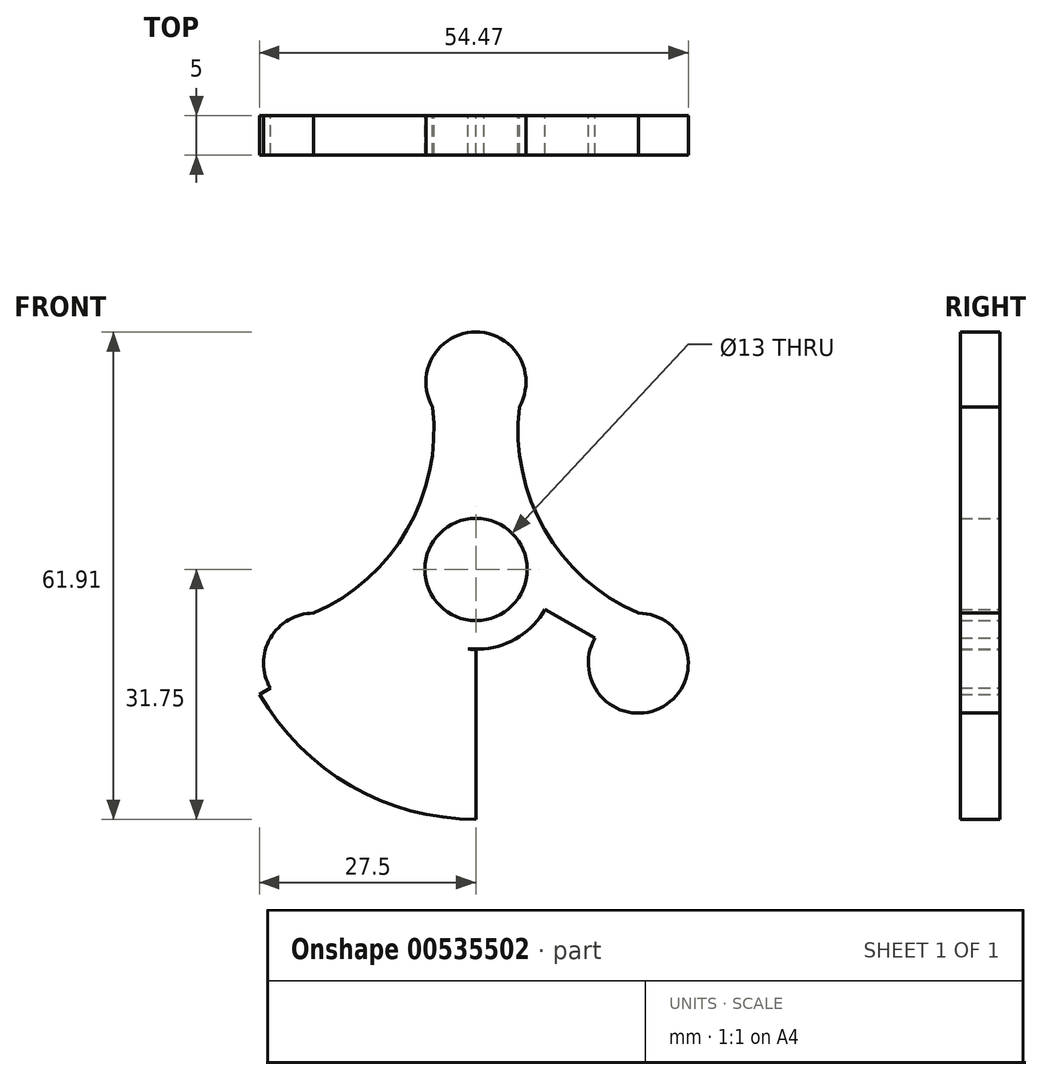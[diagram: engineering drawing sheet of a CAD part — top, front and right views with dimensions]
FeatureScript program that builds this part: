
annotation { "Feature Type Name" : "Feature", "Feature Type Description" : "" }
export const myFeature = defineFeature(function(context is Context, id is Id, definition is map)
    precondition{}
    {
        {
            var Q0;
            Q0=qCreatedBy(makeId("Front.planeOp"),FACE);
            var sketch = newSketch(context, id + "F0", { "sketchPlane" : qUnion([Q0])});
            skCircle(sketch, "E0", {"center": v(0, 0) * mm, "radius": 10.16 * mm});
            skCircle(sketch, "E1", {"center": v(0, 0) * mm, "radius": 31.75 * mm});
            skLineSegment(sketch, "E2", {"start": v(0, 0) * mm, "end": v(0, 31.75) * mm});
            skLineSegment(sketch, "E3", {"start": v(0, 0) * mm, "end": v(0, -31.75) * mm});
            skLineSegment(sketch, "E4", {"start": v(0, 0) * mm, "end": v(-31.75, 0) * mm});
            skLineSegment(sketch, "E5", {"start": v(0, 0) * mm, "end": v(31.75, 0) * mm});
            skLineSegment(sketch, "E6", {"start": v(0, -15.88) * mm, "end": v(0, -31.75) * mm});
            skLineSegment(sketch, "E7", {"start": v(15.88, 0) * mm, "end": v(31.75, 0) * mm});
            skLineSegment(sketch, "E8", {"start": v(0, 31.75) * mm, "end": v(0, 15.88) * mm});
            skLineSegment(sketch, "E9", {"start": v(-31.75, 0) * mm, "end": v(-15.88, 0) * mm});
            skPoint(sketch, "E10.endSnap0", {"position": v(0, 23.81) * mm});
            skCircle(sketch, "E11", {"center": v(0, 0) * mm, "radius": 6.5 * mm});
            skCircle(sketch, "E12", {"center": v(0, 23.81) * mm, "radius": 6.35 * mm});
            skLineSegment(sketch, "E13", {"start": v(0, 0) * mm, "end": v(-27.5, -15.87) * mm});
            skLineSegment(sketch, "E14", {"start": v(0, 0) * mm, "end": v(27.5, -15.87) * mm});
            skLineSegment(sketch, "E15", {"start": v(13.75, -7.94) * mm, "end": v(27.5, -15.87) * mm});
            skLineSegment(sketch, "E16", {"start": v(-27.5, -15.87) * mm, "end": v(-13.75, -7.94) * mm});
            skCircle(sketch, "E17", {"center": v(-20.62, -11.9) * mm, "radius": 6.35 * mm});
            skCircle(sketch, "E18", {"center": v(20.62, -11.9) * mm, "radius": 6.35 * mm});
            skLineSegment(sketch, "E19", {"start": v(-20.62, -11.9) * mm, "end": v(-23.8, -6.4) * mm});
            skLineSegment(sketch, "E20", {"start": v(-20.62, -11.9) * mm, "end": v(-20.62, -5.56) * mm});
            skLineSegment(sketch, "E21", {"start": v(-20.62, -11.9) * mm, "end": v(-15.12, -15.08) * mm});
            skLineSegment(sketch, "E22", {"start": v(20.62, -11.9) * mm, "end": v(15.12, -15.08) * mm});
            skLineSegment(sketch, "E23", {"start": v(20.62, -11.9) * mm, "end": v(20.62, -5.56) * mm});
            skLineSegment(sketch, "E24", {"start": v(0, 23.81) * mm, "end": v(-5.5, 20.64) * mm});
            skLineSegment(sketch, "E25", {"start": v(0, 23.81) * mm, "end": v(5.5, 20.64) * mm});
            skArc(sketch, "E26", {"start": v(-20.62, -5.56) * mm, "mid": v(-8.74, 5.04) * mm, "end": v(-5.5, 20.64) * mm});
            skArc(sketch, "E27", {"start": v(5.5, 20.64) * mm, "mid": v(8.74, 5.04) * mm, "end": v(20.62, -5.56) * mm});
            skArc(sketch, "E28", {"start": v(15.12, -15.08) * mm, "mid": v(0, -10.09) * mm, "end": v(-15.12, -15.08) * mm});
            skSolve(sketch);
        }
        {
            var Q0;
            {var subQ4=sQuery(id+"F0.wireOp",EDGE,"Nn59y272-KgEK-Tf1f-FvXl-cWmohsqVK5N8");Q0=makeQuery(id+"F0.imprint","IMPRINT",FACE,{"disambiguationData":[TD([[makeQuery(id+"F0.imprint","IMPRINT",EDGE,{"derivedFrom":subQ4}),-1.0]])]});}
            var Q1;
            {var subQ4=sQuery(id+"F0.wireOp",EDGE,"AeUKzeME-g7Zy-zJGz-hDGm-dAPuw4s3pSNf");Q1=makeQuery(id+"F0.imprint","IMPRINT",FACE,{"disambiguationData":[TD([[makeQuery(id+"F0.imprint","IMPRINT",EDGE,{"derivedFrom":subQ4}),1.0]])]});}
            var Q2;
            {var subQ4=sQuery(id+"F0.wireOp",EDGE,"hM1Sb0bG-RPZa-bhlv-lUgL-axLJg7qidQhS");Q2=makeQuery(id+"F0.imprint","IMPRINT",FACE,{"disambiguationData":[TD([[makeQuery(id+"F0.imprint","IMPRINT",EDGE,{"derivedFrom":subQ4}),-1.0]])]});}
            var Q3;
            {var subQ4=sQuery(id+"F0.wireOp",EDGE,"MsS3gz4T-neD6-l0GZ-bN8V-Hu56j2tn55OF");Q3=makeQuery(id+"F0.imprint","IMPRINT",FACE,{"disambiguationData":[TD([[makeQuery(id+"F0.imprint","IMPRINT",EDGE,{"derivedFrom":subQ4}),-1.0]])]});}
            var Q4;
            {var subQ3=sQuery(id+"F0.wireOp",EDGE,"E4");var subQ5=sQuery(id+"F0.wireOp",EDGE,"E11");var subQ6=makeQuery(id+"F0.imprint","INTERSECT",VERTEX,{"derivedFrom":[subQ3,subQ5]});Q4=makeQuery(id+"F0.imprint","IMPRINT",FACE,{"disambiguationData":[TD([[makeQuery(id+"F0.imprint","IMPRINT",EDGE,{"disambiguationData":[TD([[subQ6,1.0]])],"derivedFrom":subQ5}),-1.0]])]});}
            var Q5;
            {var subQ0=sQuery(id+"F0.wireOp",EDGE,"E4");var subQ5=sQuery(id+"F0.wireOp",EDGE,"E11");var subQ6=makeQuery(id+"F0.imprint","INTERSECT",VERTEX,{"derivedFrom":[subQ0,subQ5]});Q5=makeQuery(id+"F0.imprint","IMPRINT",FACE,{"disambiguationData":[TD([[makeQuery(id+"F0.imprint","IMPRINT",EDGE,{"disambiguationData":[TD([[subQ6,-1.0]])],"derivedFrom":subQ5}),-1.0]])]});}
            var Q6;
            {var subQ0=sQuery(id+"F0.wireOp",EDGE,"E3");var subQ5=sQuery(id+"F0.wireOp",EDGE,"E11");var subQ6=makeQuery(id+"F0.imprint","INTERSECT",VERTEX,{"derivedFrom":[subQ0,subQ5]});Q6=makeQuery(id+"F0.imprint","IMPRINT",FACE,{"disambiguationData":[TD([[makeQuery(id+"F0.imprint","IMPRINT",EDGE,{"disambiguationData":[TD([[subQ6,1.0]])],"derivedFrom":subQ5}),-1.0]])]});}
            var Q7;
            {var subQ0=sQuery(id+"F0.wireOp",EDGE,"E3");var subQ5=sQuery(id+"F0.wireOp",EDGE,"E11");var subQ6=makeQuery(id+"F0.imprint","INTERSECT",VERTEX,{"derivedFrom":[subQ0,subQ5]});Q7=makeQuery(id+"F0.imprint","IMPRINT",FACE,{"disambiguationData":[TD([[makeQuery(id+"F0.imprint","IMPRINT",EDGE,{"disambiguationData":[TD([[subQ6,-1.0]])],"derivedFrom":subQ5}),-1.0]])]});}
            var Q8;
            {var subQ3=sQuery(id+"F0.wireOp",EDGE,"E5");var subQ5=sQuery(id+"F0.wireOp",EDGE,"E11");var subQ6=makeQuery(id+"F0.imprint","INTERSECT",VERTEX,{"derivedFrom":[subQ3,subQ5]});Q8=makeQuery(id+"F0.imprint","IMPRINT",FACE,{"disambiguationData":[TD([[makeQuery(id+"F0.imprint","IMPRINT",EDGE,{"disambiguationData":[TD([[subQ6,1.0]])],"derivedFrom":subQ5}),-1.0]])]});}
            var Q9;
            {var subQ0=sQuery(id+"F0.wireOp",EDGE,"E5");var subQ5=sQuery(id+"F0.wireOp",EDGE,"E11");var subQ7=makeQuery(id+"F0.imprint","INTERSECT",VERTEX,{"derivedFrom":[subQ0,subQ5]});Q9=makeQuery(id+"F0.imprint","IMPRINT",FACE,{"disambiguationData":[TD([[makeQuery(id+"F0.imprint","IMPRINT",EDGE,{"disambiguationData":[TD([[subQ7,-1.0]])],"derivedFrom":subQ5}),-1.0]])]});}
            var Q10;
            {var subQ3=sQuery(id+"F0.wireOp",EDGE,"E2");var subQ5=sQuery(id+"F0.wireOp",EDGE,"E11");var subQ6=makeQuery(id+"F0.imprint","INTERSECT",VERTEX,{"derivedFrom":[subQ3,subQ5]});Q10=makeQuery(id+"F0.imprint","IMPRINT",FACE,{"disambiguationData":[TD([[makeQuery(id+"F0.imprint","IMPRINT",EDGE,{"disambiguationData":[TD([[subQ6,1.0]])],"derivedFrom":subQ5}),-1.0]])]});}
            var Q11;
            {var subQ0=sQuery(id+"F0.wireOp",EDGE,"E2");var subQ5=sQuery(id+"F0.wireOp",EDGE,"E11");var subQ6=makeQuery(id+"F0.imprint","INTERSECT",VERTEX,{"derivedFrom":[subQ0,subQ5]});Q11=makeQuery(id+"F0.imprint","IMPRINT",FACE,{"disambiguationData":[TD([[makeQuery(id+"F0.imprint","IMPRINT",EDGE,{"disambiguationData":[TD([[subQ6,-1.0]])],"derivedFrom":subQ5}),-1.0]])]});}
            var Q12;
            Q12=makeQuery(id+"F0.imprint","IMPRINT",FACE,{"disambiguationData":[TD([[makeQuery(id+"F0.imprint","IMPRINT",EDGE,{"derivedFrom":sQuery(id+"F0.wireOp",EDGE,"ooFB2VaF-3c2q-YO7V-qsAl-rdo7uhoZPCNn")}),1.0]])]});
            var Q13;
            Q13=makeQuery(id+"F0.imprint","IMPRINT",FACE,{"disambiguationData":[TD([[makeQuery(id+"F0.imprint","IMPRINT",EDGE,{"derivedFrom":sQuery(id+"F0.wireOp",EDGE,"WVsS6rBz-TdHu-QTsm-AklR-FrBDINxnMIws")}),1.0]])]});
            var Q14;
            Q14=makeQuery(id+"F0.imprint","IMPRINT",FACE,{"disambiguationData":[TD([[makeQuery(id+"F0.imprint","IMPRINT",EDGE,{"derivedFrom":sQuery(id+"F0.wireOp",EDGE,"sqomMokA-Ww9J-Kp4e-93TC-KIV9wOQSZvNW")}),1.0]])]});
            var Q15;
            Q15=makeQuery(id+"F0.imprint","IMPRINT",FACE,{"disambiguationData":[TD([[makeQuery(id+"F0.imprint","IMPRINT",EDGE,{"derivedFrom":sQuery(id+"F0.wireOp",EDGE,"JilBXdVU-ywiD-XJRb-jOZm-rQGInwL4JtPe")}),1.0]])]});
            var Q16;
            Q16=makeQuery(id+"F0.imprint","IMPRINT",FACE,{"disambiguationData":[TD([[makeQuery(id+"F0.imprint","IMPRINT",EDGE,{"derivedFrom":sQuery(id+"F0.wireOp",EDGE,"myRfCI6Q-ulPl-DbWN-DlNa-KoahSxTihuXt")}),1.0]])]});
            var Q17;
            Q17=makeQuery(id+"F0.imprint","IMPRINT",FACE,{"disambiguationData":[TD([[makeQuery(id+"F0.imprint","IMPRINT",EDGE,{"derivedFrom":sQuery(id+"F0.wireOp",EDGE,"Ojyoilpx-K28e-mgz9-RSAK-IUr9TCxTUTsy")}),1.0]])]});
            var Q18;
            Q18=makeQuery(id+"F0.imprint","IMPRINT",FACE,{"disambiguationData":[TD([[makeQuery(id+"F0.imprint","IMPRINT",EDGE,{"derivedFrom":sQuery(id+"F0.wireOp",EDGE,"qKwkJ07P-EkNn-llE7-GIzP-B0sZXtiIGCul")}),1.0]])]});
            var Q19;
            Q19=makeQuery(id+"F0.imprint","IMPRINT",FACE,{"disambiguationData":[TD([[makeQuery(id+"F0.imprint","IMPRINT",EDGE,{"derivedFrom":sQuery(id+"F0.wireOp",EDGE,"y0ZgGNou-KlNx-77Q5-BXN6-z3mfEDGF28Ua")}),1.0]])]});
            var Q20;
            {var subQ1=sQuery(id+"F0.wireOp",EDGE,"E2");var subQ6=sQuery(id+"F0.wireOp",EDGE,"E0");var subQ10=makeQuery(id+"F0.imprint","INTERSECT",VERTEX,{"derivedFrom":[subQ6,subQ1]});Q20=makeQuery(id+"F0.imprint","IMPRINT",FACE,{"disambiguationData":[TD([[makeQuery(id+"F0.imprint","IMPRINT",EDGE,{"disambiguationData":[TD([[subQ10,-1.0]])],"derivedFrom":subQ6}),-1.0]])]});}
            var Q21;
            {var subQ0=sQuery(id+"F0.wireOp",EDGE,"E24");Q21=makeQuery(id+"F0.imprint","IMPRINT",FACE,{"disambiguationData":[TD([[makeQuery(id+"F0.imprint","IMPRINT",EDGE,{"derivedFrom":subQ0}),-1.0]])]});}
            var Q22;
            {var subQ0=sQuery(id+"F0.wireOp",EDGE,"E25");Q22=makeQuery(id+"F0.imprint","IMPRINT",FACE,{"disambiguationData":[TD([[makeQuery(id+"F0.imprint","IMPRINT",EDGE,{"derivedFrom":subQ0}),1.0]])]});}
            var Q23;
            {var subQ0=sQuery(id+"F0.wireOp",EDGE,"E25");Q23=makeQuery(id+"F0.imprint","IMPRINT",FACE,{"disambiguationData":[TD([[makeQuery(id+"F0.imprint","IMPRINT",EDGE,{"derivedFrom":subQ0}),-1.0]])]});}
            var Q24;
            {var subQ0=sQuery(id+"F0.wireOp",EDGE,"E24");Q24=makeQuery(id+"F0.imprint","IMPRINT",FACE,{"disambiguationData":[TD([[makeQuery(id+"F0.imprint","IMPRINT",EDGE,{"derivedFrom":subQ0}),1.0]])]});}
            var Q25;
            {var subQ0=sQuery(id+"F0.wireOp",EDGE,"E20");Q25=makeQuery(id+"F0.imprint","IMPRINT",FACE,{"disambiguationData":[TD([[makeQuery(id+"F0.imprint","IMPRINT",EDGE,{"derivedFrom":subQ0}),-1.0]])]});}
            var Q26;
            {var subQ0=sQuery(id+"F0.wireOp",EDGE,"E19");Q26=makeQuery(id+"F0.imprint","IMPRINT",FACE,{"disambiguationData":[TD([[makeQuery(id+"F0.imprint","IMPRINT",EDGE,{"derivedFrom":subQ0}),-1.0]])]});}
            var Q27;
            {var subQ0=sQuery(id+"F0.wireOp",EDGE,"E19");Q27=makeQuery(id+"F0.imprint","IMPRINT",FACE,{"disambiguationData":[TD([[makeQuery(id+"F0.imprint","IMPRINT",EDGE,{"derivedFrom":subQ0}),1.0]])]});}
            var Q28;
            {var subQ0=sQuery(id+"F0.wireOp",EDGE,"E21");Q28=makeQuery(id+"F0.imprint","IMPRINT",FACE,{"disambiguationData":[TD([[makeQuery(id+"F0.imprint","IMPRINT",EDGE,{"derivedFrom":subQ0}),-1.0]])]});}
            var Q29;
            {var subQ0=sQuery(id+"F0.wireOp",EDGE,"E21");Q29=makeQuery(id+"F0.imprint","IMPRINT",FACE,{"disambiguationData":[TD([[makeQuery(id+"F0.imprint","IMPRINT",EDGE,{"derivedFrom":subQ0}),1.0]])]});}
            var Q30;
            {var subQ0=sQuery(id+"F0.wireOp",EDGE,"E22");Q30=makeQuery(id+"F0.imprint","IMPRINT",FACE,{"disambiguationData":[TD([[makeQuery(id+"F0.imprint","IMPRINT",EDGE,{"derivedFrom":subQ0}),1.0]])]});}
            var Q31;
            {var subQ0=sQuery(id+"F0.wireOp",EDGE,"E23");Q31=makeQuery(id+"F0.imprint","IMPRINT",FACE,{"disambiguationData":[TD([[makeQuery(id+"F0.imprint","IMPRINT",EDGE,{"derivedFrom":subQ0}),-1.0]])]});}
            var Q32;
            {var subQ0=sQuery(id+"F0.wireOp",EDGE,"E23");Q32=makeQuery(id+"F0.imprint","IMPRINT",FACE,{"disambiguationData":[TD([[makeQuery(id+"F0.imprint","IMPRINT",EDGE,{"derivedFrom":subQ0}),1.0]])]});}
            var Q33;
            {var subQ0=sQuery(id+"F0.wireOp",EDGE,"E22");Q33=makeQuery(id+"F0.imprint","IMPRINT",FACE,{"disambiguationData":[TD([[makeQuery(id+"F0.imprint","IMPRINT",EDGE,{"derivedFrom":subQ0}),-1.0]])]});}
            var Q34;
            {var subQ1=sQuery(id+"F0.wireOp",EDGE,"E13");var subQ3=sQuery(id+"F0.wireOp",EDGE,"E0");var subQ4=makeQuery(id+"F0.imprint","INTERSECT",VERTEX,{"derivedFrom":[subQ3,subQ1]});Q34=makeQuery(id+"F0.imprint","IMPRINT",FACE,{"disambiguationData":[TD([[makeQuery(id+"F0.imprint","IMPRINT",EDGE,{"disambiguationData":[TD([[subQ4,-1.0]])],"derivedFrom":subQ3}),-1.0]])]});}
            var Q35;
            {var subQ1=sQuery(id+"F0.wireOp",EDGE,"E2");var subQ5=sQuery(id+"F0.wireOp",EDGE,"E0");var subQ6=makeQuery(id+"F0.imprint","INTERSECT",VERTEX,{"derivedFrom":[subQ5,subQ1]});Q35=makeQuery(id+"F0.imprint","IMPRINT",FACE,{"disambiguationData":[TD([[makeQuery(id+"F0.imprint","IMPRINT",EDGE,{"disambiguationData":[TD([[subQ6,1.0]])],"derivedFrom":subQ5}),-1.0]])]});}
            var Q36;
            {var subQ3=sQuery(id+"F0.wireOp",EDGE,"E0");var subQ5=sQuery(id+"F0.wireOp",EDGE,"E5");var subQ6=makeQuery(id+"F0.imprint","INTERSECT",VERTEX,{"derivedFrom":[subQ3,subQ5]});Q36=makeQuery(id+"F0.imprint","IMPRINT",FACE,{"disambiguationData":[TD([[makeQuery(id+"F0.imprint","IMPRINT",EDGE,{"disambiguationData":[TD([[subQ6,1.0]])],"derivedFrom":subQ3}),-1.0]])]});}
            var Q37;
            {var subQ3=sQuery(id+"F0.wireOp",EDGE,"E0");var subQ7=sQuery(id+"F0.wireOp",EDGE,"E4");var subQ8=makeQuery(id+"F0.imprint","INTERSECT",VERTEX,{"derivedFrom":[subQ3,subQ7]});Q37=makeQuery(id+"F0.imprint","IMPRINT",FACE,{"disambiguationData":[TD([[makeQuery(id+"F0.imprint","IMPRINT",EDGE,{"disambiguationData":[TD([[subQ8,-1.0]])],"derivedFrom":subQ3}),-1.0]])]});}
            var Q38;
            {var subQ5=sQuery(id+"F0.wireOp",EDGE,"E28");var subQ7=sQuery(id+"F0.wireOp",EDGE,"E0");var subQ9=makeQuery(id+"F0.imprint","INTERSECT",VERTEX,{"disambiguationData":[OD(1.0)],"derivedFrom":[subQ7,subQ5]});Q38=makeQuery(id+"F0.imprint","IMPRINT",FACE,{"disambiguationData":[TD([[makeQuery(id+"F0.imprint","IMPRINT",EDGE,{"disambiguationData":[TD([[subQ9,-1.0]])],"derivedFrom":subQ7}),-1.0]])]});}
            var Q39;
            {var subQ0=sQuery(id+"F0.wireOp",EDGE,"E26");var subQ1=sQuery(id+"F0.wireOp",EDGE,"E0");var subQ2=makeQuery(id+"F0.imprint","INTERSECT",VERTEX,{"disambiguationData":[OD(1.0)],"derivedFrom":[subQ1,subQ0]});Q39=makeQuery(id+"F0.imprint","IMPRINT",FACE,{"disambiguationData":[TD([[makeQuery(id+"F0.imprint","IMPRINT",EDGE,{"disambiguationData":[TD([[subQ2,-1.0]])],"derivedFrom":subQ1}),-1.0]])]});}
            var Q40;
            {var subQ0=sQuery(id+"F0.wireOp",EDGE,"E27");var subQ1=sQuery(id+"F0.wireOp",EDGE,"E0");var subQ2=makeQuery(id+"F0.imprint","INTERSECT",VERTEX,{"disambiguationData":[OD(0.0)],"derivedFrom":[subQ1,subQ0]});Q40=makeQuery(id+"F0.imprint","IMPRINT",FACE,{"disambiguationData":[TD([[makeQuery(id+"F0.imprint","IMPRINT",EDGE,{"disambiguationData":[TD([[subQ2,1.0]])],"derivedFrom":subQ1}),-1.0]])]});}
            extrude(context, id + "F1", {"entities" : qUnion([Q0, Q1, Q2, Q3, Q4, Q5, Q6, Q7, Q8, Q9, Q10, Q11, Q12, Q13, Q14, Q15, Q16, Q17, Q18, Q19, Q20, Q21, Q22, Q23, Q24, Q25, Q26, Q27, Q28, Q29, Q30, Q31, Q32, Q33, Q34, Q35, Q36, Q37, Q38, Q39, Q40]), "depth" : 5 * mm, "offsetDistance" : 25.4 * mm});
        }
    });
